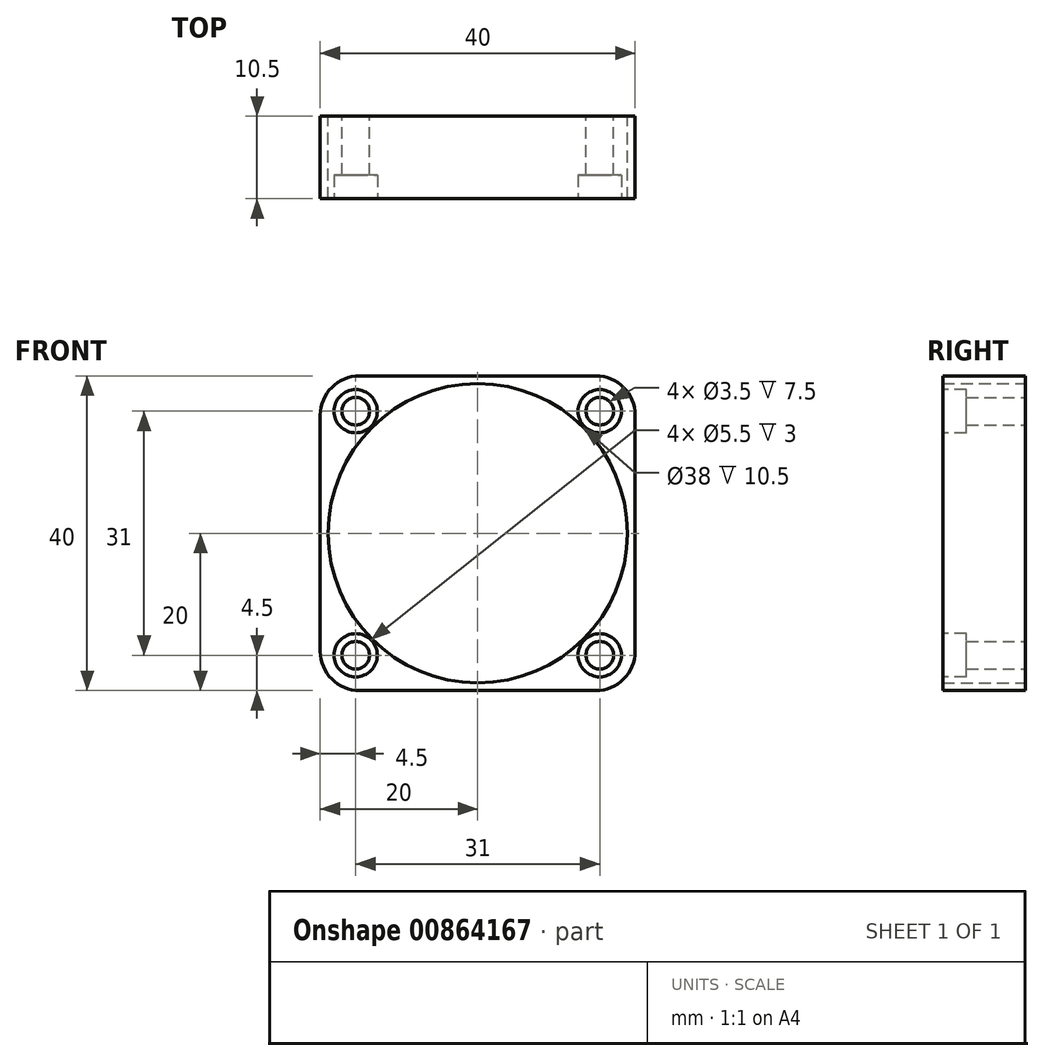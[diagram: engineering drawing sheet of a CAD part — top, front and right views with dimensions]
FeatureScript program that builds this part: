
annotation { "Feature Type Name" : "Feature", "Feature Type Description" : "" }
export const myFeature = defineFeature(function(context is Context, id is Id, definition is map)
    precondition{}
    {
        {
            var Q0;
            Q0=qCreatedBy(makeId("Front.planeOp"),FACE);
            var sketch = newSketch(context, id + "F0", { "sketchPlane" : qUnion([Q0])});
            skLineSegment(sketch, "E0.bottom", {"start": v(20, 20) * mm, "end": v(-20, 20) * mm});
            skLineSegment(sketch, "E0.top", {"start": v(20, -20) * mm, "end": v(-20, -20) * mm});
            skLineSegment(sketch, "E0.left", {"start": v(20, 20) * mm, "end": v(20, -20) * mm});
            skLineSegment(sketch, "E0.right", {"start": v(-20, 20) * mm, "end": v(-20, -20) * mm});
            skPoint(sketch, "E0.middle", {"position": v(0, 0) * mm});
            skLineSegment(sketch, "E1.bottom", {"start": v(15.5, 15.5) * mm, "end": v(-15.5, 15.5) * mm, "construction": true});
            skLineSegment(sketch, "E1.top", {"start": v(15.5, -15.5) * mm, "end": v(-15.5, -15.5) * mm, "construction": true});
            skLineSegment(sketch, "E1.left", {"start": v(15.5, 15.5) * mm, "end": v(15.5, -15.5) * mm, "construction": true});
            skLineSegment(sketch, "E1.right", {"start": v(-15.5, 15.5) * mm, "end": v(-15.5, -15.5) * mm, "construction": true});
            skCircle(sketch, "E2", {"center": v(0, 0) * mm, "radius": 19 * mm});
            skCircle(sketch, "E3", {"center": v(15.5, 15.5) * mm, "radius": 1.75 * mm});
            skCircle(sketch, "E4", {"center": v(-15.5, 15.5) * mm, "radius": 1.75 * mm});
            skCircle(sketch, "E5", {"center": v(-15.5, -15.5) * mm, "radius": 1.75 * mm});
            skCircle(sketch, "E6", {"center": v(15.5, -15.5) * mm, "radius": 1.75 * mm});
            skSolve(sketch);
        }
        {
            var Q0;
            Q0 = qSketchRegion(id + "F0", true);
            extrude(context, id + "F1", {"entities" : qUnion([Q0]), "depth" : 10.5 * mm, "offsetDistance" : 25 * mm});
        }
        {
            var Q0;
            Q0=makeQuery(id+"F1.opExtrude","CAP_FACE",FACE,{"disambiguationData":[OSD([sQuery(id+"F0.wireOp",EDGE,"E0.bottom"),sQuery(id+"F0.wireOp",EDGE,"E0.top"),sQuery(id+"F0.wireOp",EDGE,"E0.left"),sQuery(id+"F0.wireOp",EDGE,"E0.right"),sQuery(id+"F0.wireOp",EDGE,"E2"),sQuery(id+"F0.wireOp",EDGE,"E3"),sQuery(id+"F0.wireOp",EDGE,"E4"),sQuery(id+"F0.wireOp",EDGE,"E5"),sQuery(id+"F0.wireOp",EDGE,"E6")])],"isStart":false});
            var sketch = newSketch(context, id + "F2", { "sketchPlane" : qUnion([Q0])});
            skCircle(sketch, "E7", {"center": v(-15.5, 15.5) * mm, "radius": 2.75 * mm});
            skCircle(sketch, "E8", {"center": v(15.5, 15.5) * mm, "radius": 2.75 * mm});
            skCircle(sketch, "E9", {"center": v(15.5, -15.5) * mm, "radius": 2.75 * mm});
            skCircle(sketch, "E10", {"center": v(-15.5, -15.5) * mm, "radius": 2.75 * mm});
            skSolve(sketch);
        }
        {
            var Q0;
            Q0 = qSketchRegion(id + "F2", true);
            extrude(context, id + "F3", {"entities" : qUnion([Q0]), "operationType" : NewBodyOperationType.REMOVE, "oppositeDirection" : true, "depth" : 3 * mm, "offsetDistance" : 25 * mm});
        }
        {
            var Q0;
            Q0=makeQuery(id+"F1.opExtrude","SWEPT_EDGE",EDGE,{"disambiguationData":[OSD([sQuery(id+"F0.wireOp",EDGE,"E0.bottom"),sQuery(id+"F0.wireOp",EDGE,"E0.left")])]});
            var Q1;
            Q1=makeQuery(id+"F1.opExtrude","SWEPT_EDGE",EDGE,{"disambiguationData":[OSD([sQuery(id+"F0.wireOp",EDGE,"E0.bottom"),sQuery(id+"F0.wireOp",EDGE,"E0.right")])]});
            var Q2;
            Q2=makeQuery(id+"F1.opExtrude","SWEPT_EDGE",EDGE,{"disambiguationData":[OSD([sQuery(id+"F0.wireOp",EDGE,"E0.top"),sQuery(id+"F0.wireOp",EDGE,"E0.right")])]});
            var Q3;
            Q3=makeQuery(id+"F1.opExtrude","SWEPT_EDGE",EDGE,{"disambiguationData":[OSD([sQuery(id+"F0.wireOp",EDGE,"E0.top"),sQuery(id+"F0.wireOp",EDGE,"E0.left")])]});
            fillet(context, id + "F4", {"entities" : qUnion([Q0, Q1, Q2, Q3]), "radius" : 5 * mm, "tangentPropagation" : true, "allowEdgeOverflow" : false});
        }
    });
